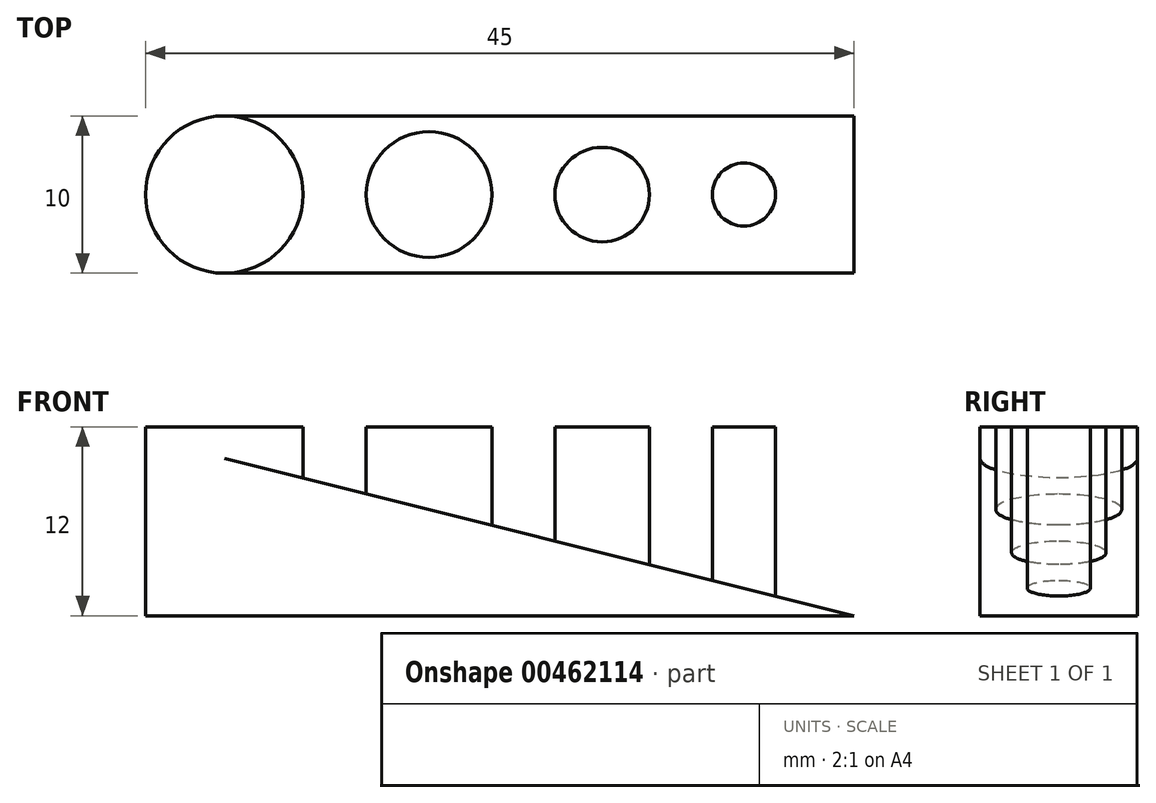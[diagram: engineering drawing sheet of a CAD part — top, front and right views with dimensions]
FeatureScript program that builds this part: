
annotation { "Feature Type Name" : "Feature", "Feature Type Description" : "" }
export const myFeature = defineFeature(function(context is Context, id is Id, definition is map)
    precondition{}
    {
        {
            var Q0;
            Q0=qCreatedBy(makeId("Top.planeOp"),FACE);
            var sketch = newSketch(context, id + "F0", { "sketchPlane" : qUnion([Q0])});
            skLineSegment(sketch, "E0.bottom", {"start": v(0, 0) * mm, "end": v(40, 0) * mm});
            skLineSegment(sketch, "E0.top", {"start": v(0, -10) * mm, "end": v(40, -10) * mm});
            skLineSegment(sketch, "E0.left", {"start": v(0, 0) * mm, "end": v(0, -10) * mm});
            skLineSegment(sketch, "E0.right", {"start": v(40, 0) * mm, "end": v(40, -10) * mm});
            skSolve(sketch);
        }
        {
            var Q0;
            Q0 = qSketchRegion(id + "F0", true);
            extrude(context, id + "F1", {"entities" : qUnion([Q0]), "depth" : 10 * mm});
        }
        {
            var Q0;
            Q0=makeQuery(id+"F1.opExtrude","SWEPT_FACE",FACE,{"disambiguationData":[OSD([sQuery(id+"F0.wireOp",EDGE,"E0.top")])]});
            var sketch = newSketch(context, id + "F2", { "sketchPlane" : qUnion([Q0])});
            skLineSegment(sketch, "E1", {"start": v(0, 10) * mm, "end": v(40, 0) * mm});
            skLineSegment(sketch, "E2", {"start": v(40, 0) * mm, "end": v(40, 10) * mm});
            skLineSegment(sketch, "E3", {"start": v(40, 10) * mm, "end": v(0, 10) * mm});
            skSolve(sketch);
        }
        {
            var Q0;
            Q0 = qSketchRegion(id + "F2", true);
            extrude(context, id + "F3", {"entities" : qUnion([Q0]), "operationType" : NewBodyOperationType.REMOVE, "oppositeDirection" : true, "depth" : 25 * mm});
        }
        {
            var Q0;
            Q0=makeQuery(id+"F1.opExtrude","CAP_FACE",FACE,{"disambiguationData":[OSD([sQuery(id+"F0.wireOp",EDGE,"E0.bottom"),sQuery(id+"F0.wireOp",EDGE,"E0.top"),sQuery(id+"F0.wireOp",EDGE,"E0.left"),sQuery(id+"F0.wireOp",EDGE,"E0.right")])],"isStart":true});
            var sketch = newSketch(context, id + "F4", { "sketchPlane" : qUnion([Q0])});
            skCircle(sketch, "E4", {"center": v(0, 5) * mm, "radius": 5 * mm});
            skCircle(sketch, "E5", {"center": v(33, 5) * mm, "radius": 2 * mm});
            skPoint(sketch, "E5.centerSnap0", {"position": v(40, 5) * mm});
            skCircle(sketch, "E6", {"center": v(13, 5) * mm, "radius": 4 * mm});
            skCircle(sketch, "E7", {"center": v(24, 5) * mm, "radius": 3 * mm});
            skLineSegment(sketch, "E8", {"start": v(5, 5) * mm, "end": v(9, 5) * mm, "construction": true});
            skLineSegment(sketch, "E9", {"start": v(17, 5) * mm, "end": v(21, 5) * mm, "construction": true});
            skLineSegment(sketch, "E10", {"start": v(27, 5) * mm, "end": v(31, 5) * mm, "construction": true});
            skSolve(sketch);
        }
        {
            var Q0;
            Q0 = qSketchRegion(id + "F4", true);
            extrude(context, id + "F5", {"entities" : qUnion([Q0]), "operationType" : NewBodyOperationType.ADD, "oppositeDirection" : true, "depth" : 12 * mm});
        }
    });
